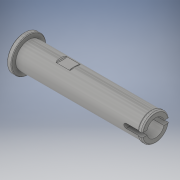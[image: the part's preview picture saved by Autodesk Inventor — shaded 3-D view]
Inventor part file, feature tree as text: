
AUTODESK INVENTOR PART (.ipt)
format: ipt  version: 2019 (Build 230136000, 136)  size: 259,584 bytes
history: native  units: mm
features: sketch x1, revolve x1, extrude x1, fillet x1
ambient origin geometry x8: Origin, YZ Plane, XZ Plane, XY Plane, X Axis, Y Axis, Z Axis, Center Point
bodies: Solid1 (feature_tree)
feature tree (4):
  sketch  "Sketch1"  dims[d0=24.0mm d1=5.0mm d2=0.8mm d3=4.8mm d4=6.4mm d5=0.8mm d6=3.2mm d7=2.8mm d8=8.0mm d9=8.0mm d10=3.4mm d11=0.8mm d12=0.4mm d13=90.0deg d14=10.0mm d15=0.0mm d16=0.1mm d17=0.2mm d18=2.4mm d19=0.2mm d20=0.2mm]
  revolve  "Revolution1"  [1 undecoded]
  extrude  "Extrusion1"  Depth=0.8mm
  fillet  "Fillet1"  Radius=4.8mm
note: 1 required parameter value undecoded (feature->parameter linkage not recoverable at this tier; creation-order binding heuristic only, values carry confidence <= 0.55)
